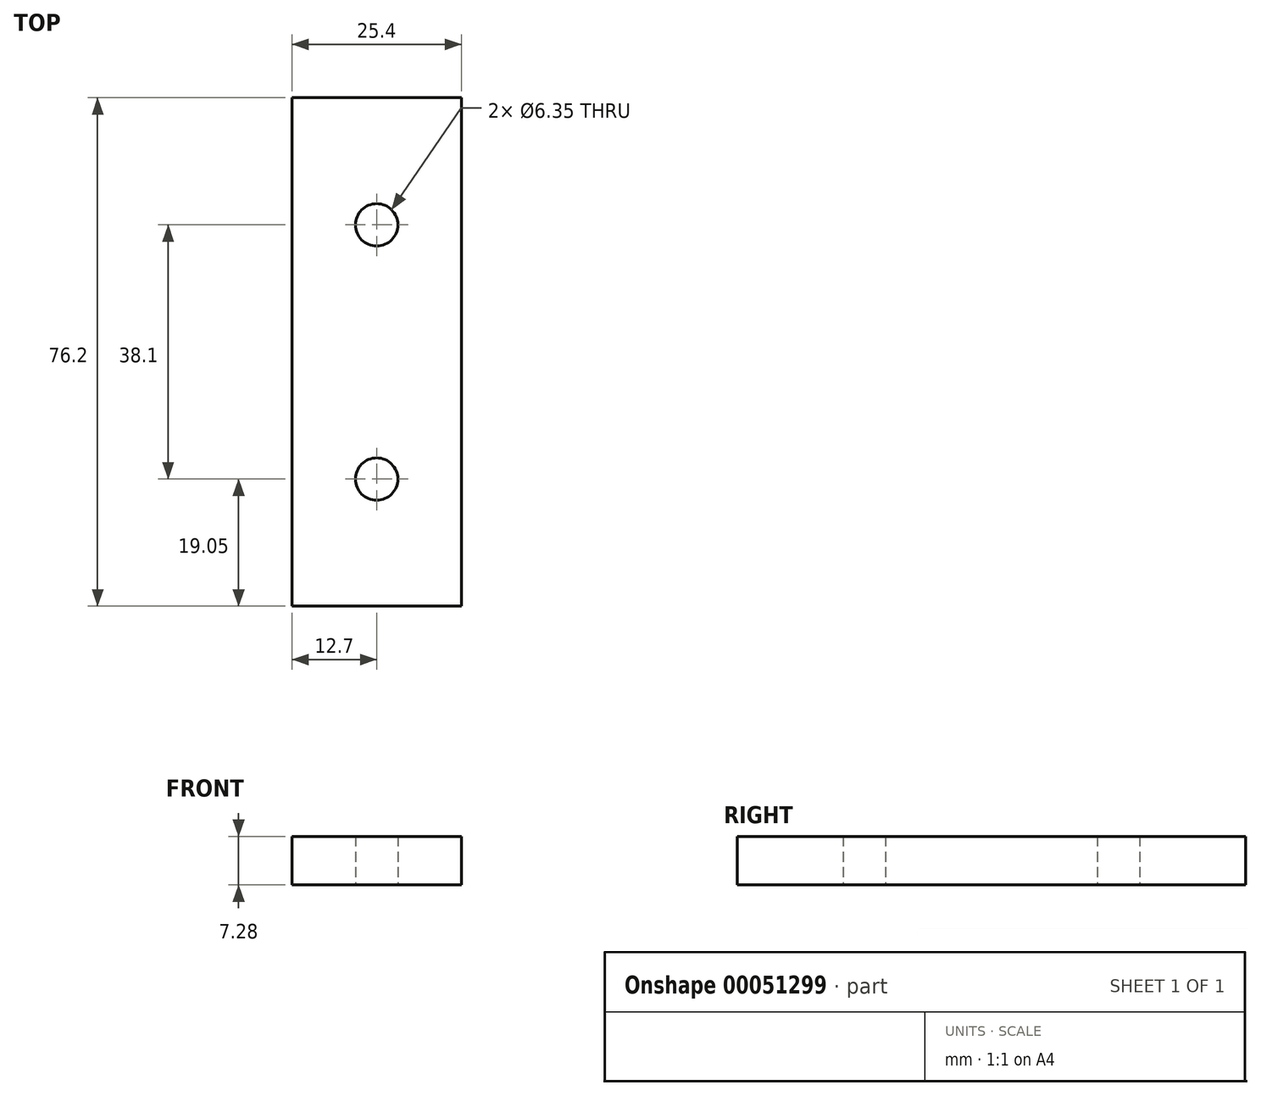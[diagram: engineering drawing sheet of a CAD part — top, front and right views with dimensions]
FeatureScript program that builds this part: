
annotation { "Feature Type Name" : "Feature", "Feature Type Description" : "" }
export const myFeature = defineFeature(function(context is Context, id is Id, definition is map)
    precondition{}
    {
        {
            var Q0;
            Q0=qCreatedBy(makeId("Top.planeOp"),FACE);
            var sketch = newSketch(context, id + "F0", { "sketchPlane" : qUnion([Q0])});
            skLineSegment(sketch, "E0", {"start": v(0, 0) * mm, "end": v(-25.4, 0) * mm});
            skLineSegment(sketch, "E1", {"start": v(-25.4, 0) * mm, "end": v(-25.4, -76.2) * mm});
            skLineSegment(sketch, "E2", {"start": v(-25.4, -76.2) * mm, "end": v(0, -76.2) * mm});
            skLineSegment(sketch, "E3", {"start": v(0, -76.2) * mm, "end": v(0, 0) * mm});
            skLineSegment(sketch, "E4", {"start": v(-12.7, 0) * mm, "end": v(-12.7, -19.05) * mm});
            skPoint(sketch, "E4.endSnap0", {"position": v(-12.7, 0) * mm});
            skLineSegment(sketch, "E5", {"start": v(-12.7, -76.2) * mm, "end": v(-12.7, -57.15) * mm});
            skSolve(sketch);
        }
        {
            var Q0;
            {var subQ1=sQuery(id+"F0.wireOp",EDGE,"E1");Q0=makeQuery(id+"F0.imprint","IMPRINT",FACE,{"disambiguationData":[TD([[makeQuery(id+"F0.imprint","IMPRINT",EDGE,{"derivedFrom":subQ1}),1.0]])]});}
            extrude(context, id + "F1", {"entities" : qUnion([Q0]), "depth" : 7.28 * mm});
        }
        {
            var Q0;
            Q0=makeQuery(id+"F1.opExtrude","CAP_FACE",FACE,{"disambiguationData":[OSD([sQuery(id+"F0.wireOp",EDGE,"E0"),sQuery(id+"F0.wireOp",EDGE,"E1"),sQuery(id+"F0.wireOp",EDGE,"E2"),sQuery(id+"F0.wireOp",EDGE,"E3")])],"isStart":true});
            var sketch = newSketch(context, id + "F2", { "sketchPlane" : qUnion([Q0])});
            skLineSegment(sketch, "E6", {"start": v(-12.7, 0) * mm, "end": v(-12.7, 19.05) * mm});
            skLineSegment(sketch, "E7", {"start": v(-12.7, 76.2) * mm, "end": v(-12.7, 57.15) * mm});
            skPoint(sketch, "E7.endSnap0", {"position": v(-12.7, 76.2) * mm});
            skSolve(sketch);
        }
        {
            var Q0;
            Q0=sQuery(id+"F2.wireOp",VERTEX,"E7.end");
            var Q1;
            Q1=makeQuery(id+"F1.opExtrude","SWEPT_BODY",BODY,{"disambiguationData":[OSD([sQuery(id+"F0.wireOp",EDGE,"E0"),sQuery(id+"F0.wireOp",EDGE,"E1"),sQuery(id+"F0.wireOp",EDGE,"E2"),sQuery(id+"F0.wireOp",EDGE,"E3")])]});
            hole(context, id + "F3", {"style" : HoleStyle.SIMPLE, "holeDiameter" : 6.35 * mm, "endStyle" : HoleEndStyle.THROUGH, "locations" : qUnion([Q0]), "scope" : qUnion([Q1])});
        }
        {
            var Q0;
            Q0=makeQuery(id+"F1.opExtrude","CAP_FACE",FACE,{"disambiguationData":[OSD([sQuery(id+"F0.wireOp",EDGE,"E0"),sQuery(id+"F0.wireOp",EDGE,"E1"),sQuery(id+"F0.wireOp",EDGE,"E2"),sQuery(id+"F0.wireOp",EDGE,"E3")])],"isStart":true});
            var sketch = newSketch(context, id + "F4", { "sketchPlane" : qUnion([Q0])});
            skLineSegment(sketch, "E8", {"start": v(-12.7, 0) * mm, "end": v(-12.7, 19.05) * mm});
            skSolve(sketch);
        }
        {
            var Q0;
            Q0=sQuery(id+"F4.wireOp",VERTEX,"E8.end");
            var Q1;
            Q1=makeQuery(id+"F1.opExtrude","SWEPT_BODY",BODY,{"disambiguationData":[OSD([sQuery(id+"F0.wireOp",EDGE,"E0"),sQuery(id+"F0.wireOp",EDGE,"E1"),sQuery(id+"F0.wireOp",EDGE,"E2"),sQuery(id+"F0.wireOp",EDGE,"E3")])]});
            hole(context, id + "F5", {"style" : HoleStyle.SIMPLE, "holeDiameter" : 6.35 * mm, "endStyle" : HoleEndStyle.THROUGH, "locations" : qUnion([Q0]), "scope" : qUnion([Q1])});
        }
    });
